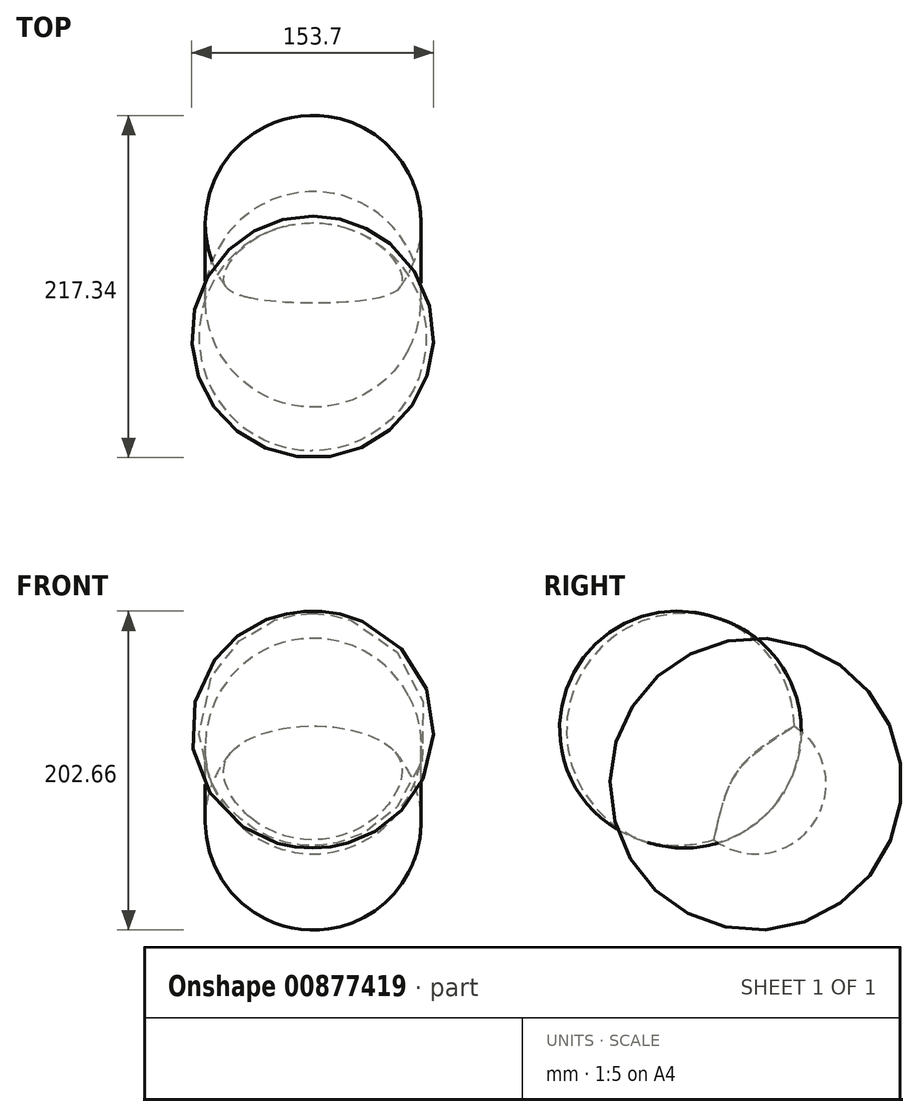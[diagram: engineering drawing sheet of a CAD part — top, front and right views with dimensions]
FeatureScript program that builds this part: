
annotation { "Feature Type Name" : "Feature", "Feature Type Description" : "" }
export const myFeature = defineFeature(function(context is Context, id is Id, definition is map)
    precondition{}
    {
        {
            var Q0;
            Q0=qCreatedBy(makeId("Top.planeOp"),FACE);
            var sketch = newSketch(context, id + "F0", { "sketchPlane" : qUnion([Q0])});
            skLineSegment(sketch, "E0", {"start": v(-63.79, 0) * mm, "end": v(64.38, 0) * mm});
            skArc(sketch, "E1", {"start": v(64.38, 0) * mm, "mid": v(0.3, 44.3) * mm, "end": v(-63.79, 0) * mm});
            skSolve(sketch);
        }
        {
            var Q0;
            Q0 = qSketchRegion(id + "F0", true);
            var Q1;
            Q1=sQuery(id+"F0.wireOp",EDGE,"E0");
            revolve(context, id + "F1", {"surfaceOperationType" : NewSurfaceOperationType.NEW, "entities" : qUnion([Q0]), "axis" : qUnion([Q1]), "revolveType" : RevolveType.FULL});
        }
        {
            var Q0;
            Q0=qCreatedBy(makeId("Right.planeOp"),FACE);
            var sketch = newSketch(context, id + "F2", { "sketchPlane" : qUnion([Q0])});
            skLineSegment(sketch, "E2", {"start": v(-24.65, 105.5) * mm, "end": v(-71.15, -36.12) * mm});
            skArc(sketch, "E3", {"start": v(-24.65, 105.5) * mm, "mid": v(-116.56, 57.23) * mm, "end": v(-71.15, -36.12) * mm});
            skSolve(sketch);
        }
        {
            var Q0;
            Q0=makeQuery(id+"F2.imprint","IMPRINT",FACE,{"disambiguationData":[TD([[makeQuery(id+"F2.imprint","IMPRINT",EDGE,{"derivedFrom":sQuery(id+"F2.wireOp",EDGE,"E2")}),-1.0]])]});
            var Q1;
            Q1=sQuery(id+"F2.wireOp",EDGE,"E2");
            revolve(context, id + "F3", {"operationType" : NewBodyOperationType.ADD, "surfaceOperationType" : NewSurfaceOperationType.NEW, "entities" : qUnion([Q0]), "axis" : qUnion([Q1]), "revolveType" : RevolveType.FULL});
        }
    });
